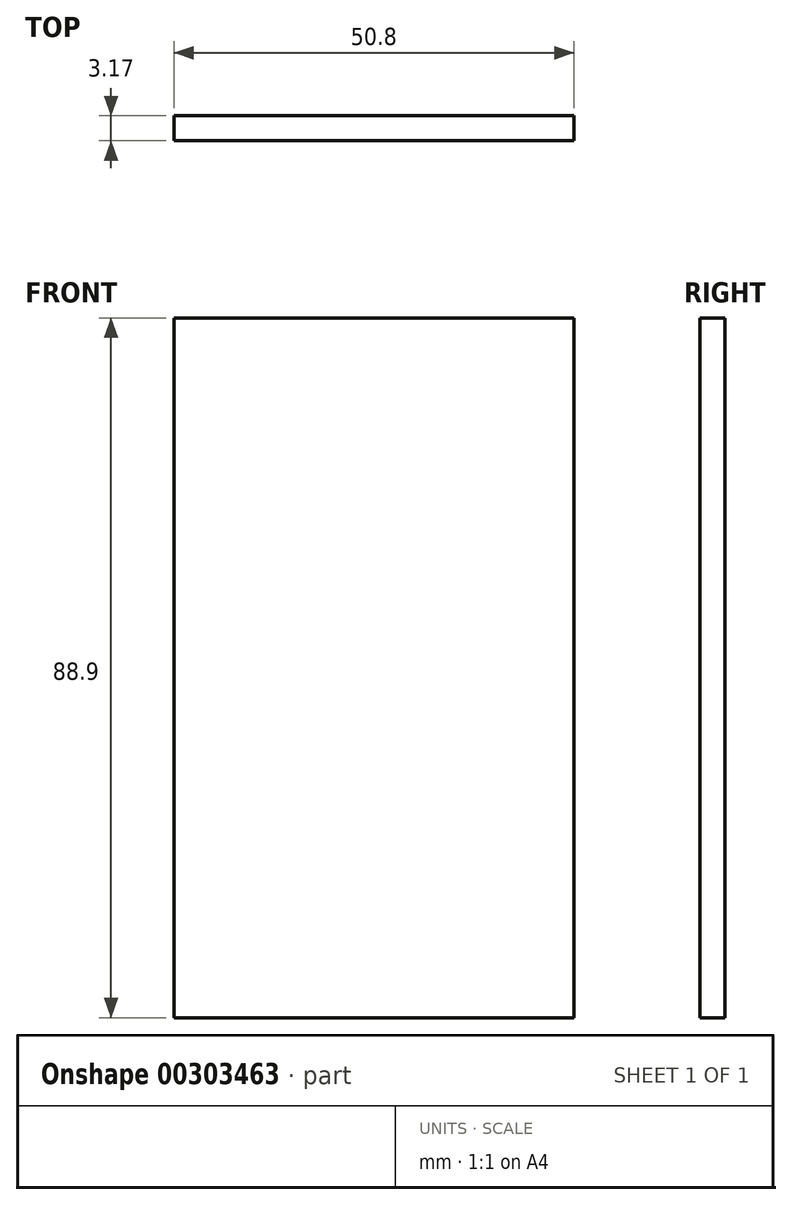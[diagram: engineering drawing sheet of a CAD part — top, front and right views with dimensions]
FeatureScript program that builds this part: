
annotation { "Feature Type Name" : "Feature", "Feature Type Description" : "" }
export const myFeature = defineFeature(function(context is Context, id is Id, definition is map)
    precondition{}
    {
        {
            var Q0;
            Q0=qCreatedBy(makeId("Front.planeOp"),FACE);
            var sketch = newSketch(context, id + "F0", { "sketchPlane" : qUnion([Q0])});
            skLineSegment(sketch, "E0.bottom", {"start": v(25.4, 44.45) * mm, "end": v(-25.4, 44.45) * mm});
            skLineSegment(sketch, "E0.top", {"start": v(25.4, -44.45) * mm, "end": v(-25.4, -44.45) * mm});
            skLineSegment(sketch, "E0.left", {"start": v(25.4, 44.45) * mm, "end": v(25.4, -44.45) * mm});
            skLineSegment(sketch, "E0.right", {"start": v(-25.4, 44.45) * mm, "end": v(-25.4, -44.45) * mm});
            skPoint(sketch, "E0.middle", {"position": v(0, 0) * mm});
            skSolve(sketch);
        }
        {
            var Q0;
            Q0 = qSketchRegion(id + "F0", true);
            extrude(context, id + "F1", {"entities" : qUnion([Q0]), "depth" : 3.17 * mm});
        }
    });
